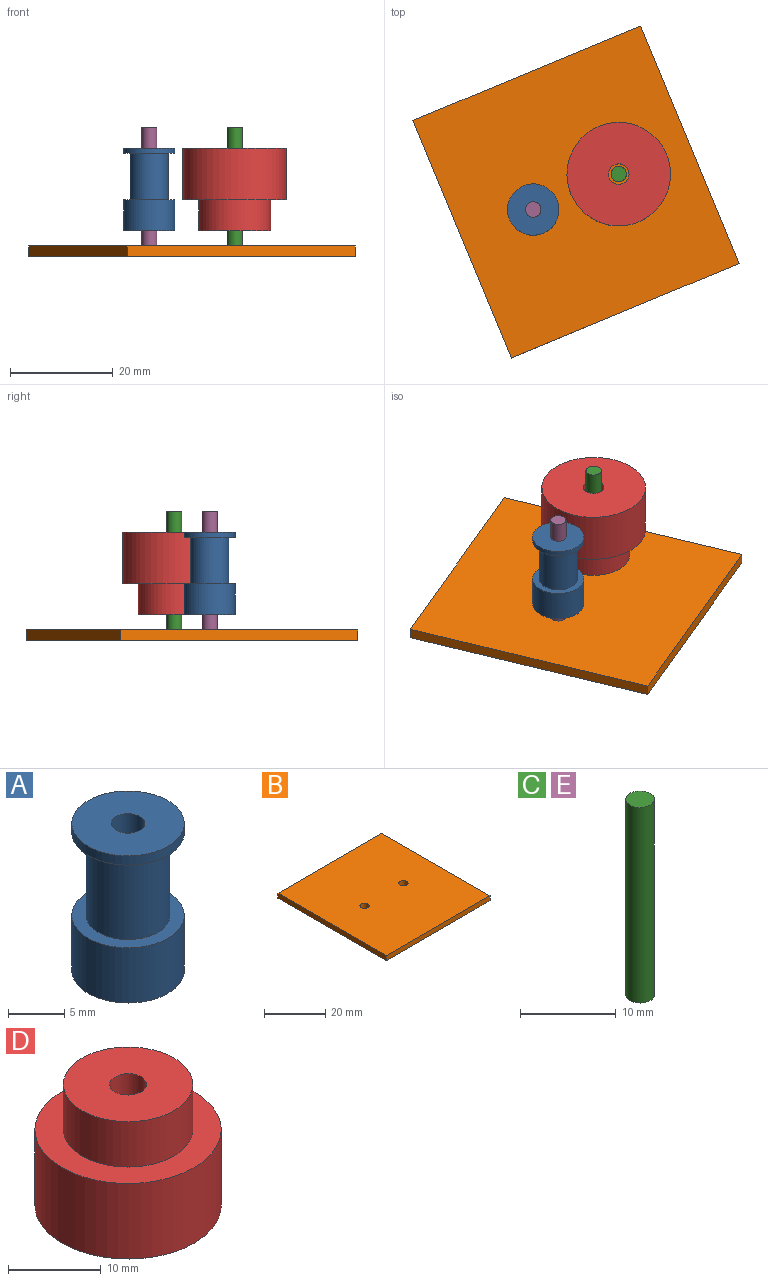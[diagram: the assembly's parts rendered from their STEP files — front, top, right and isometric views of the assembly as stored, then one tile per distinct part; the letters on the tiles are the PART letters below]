
ASSEMBLY  parts=5 mates=4
PART A: 8 faces, bbox 10x10x16 mm
  f0: cylinder r=3.73mm len=9mm, axis (0,0,1), area 210.6mm2, adj f3,f5
  f1: cylinder r=5mm len=10mm, axis (0,0,-1), area 188.5mm2, adj f2,f3
  f2: plane 10x10mm, normal (0,0,-1), area 71.5mm2, adj f1,f7
  f3: plane 10x10mm, normal (0,0,1), area 34.9mm2, adj f0,f1
  f4: cylinder r=5mm len=10mm, axis (0,0,1), area 31.4mm2, adj f5,f6
  f5: plane 10x10mm, normal (0,0,-1), area 34.9mm2, adj f0,f4
  f6: plane 10x10mm, normal (0,0,1), area 71.5mm2, adj f4,f7
  f7: cylinder r=1.5mm len=16mm, axis (0,0,1), area 150.8mm2, adj f2,f6
PART B: 8 faces, bbox 48x50x2 mm
  f0: plane 50x2mm, normal (-1,0,0), area 100mm2, adj f1,f5,f6,f7
  f1: plane 48x2mm, normal (0,1,0), area 96mm2, adj f0,f2,f6,f7
  f2: plane 50x2mm, normal (1,0,0), area 100mm2, adj f1,f5,f6,f7
  f3: cylinder r=1.5mm len=3mm, axis (0,0,1), area 18.8mm2, adj f6,f7
  f4: cylinder r=1.5mm len=3mm, axis (0,0,1), area 18.8mm2, adj f6,f7
  f5: plane 48x2mm, normal (0,-1,0), area 96mm2, adj f0,f2,f6,f7
  f6: plane 50x48mm, normal (0,0,-1), area 2385.9mm2, adj f0,f1,f2,f3,f4,f5
  f7: plane 50x48mm, normal (0,0,1), area 2385.9mm2, adj f0,f1,f2,f3,f4,f5
PART C: 3 faces, bbox 3x3x25 mm
  f0: cylinder r=1.5mm len=25mm, axis (0,0,-1), area 235.6mm2, adj f1,f2
  f1: plane 3x3mm, normal (0,0,1), area 7.1mm2, adj f0
  f2: plane 3x3mm, normal (0,0,-1), area 7.1mm2, adj f0
PART D: 6 faces, bbox 20.2x20.2x16 mm
  f0: cylinder r=10.08mm len=20.15mm, axis (0,0,-1), area 633mm2, adj f1,f3
  f1: plane 20.15x20.15mm, normal (0,0,-1), area 306.3mm2, adj f0,f5
  f2: cylinder r=7mm len=14mm, axis (0,0,1), area 263.9mm2, adj f3,f4
  f3: plane 20.15x20.15mm, normal (0,0,1), area 165mm2, adj f0,f2
  f4: plane 14x14mm, normal (0,0,1), area 141.4mm2, adj f2,f5
  f5: cylinder r=2mm len=16mm, axis (0,0,1), area 201.1mm2, adj f1,f4
PART E: same geometry as C
PLACE A t=(2.21,-9.82,-24.65)mm
PLACE B rot(axis=(0,0,-1),157.5deg) t=(10.53,-6.37,-29.65)mm
PLACE C t=(18.84,-2.92,-29.65)mm
PLACE D rot(axis=(0.2,-0.98,0),180deg) t=(18.84,-2.92,-8.65)mm
PLACE E rot(axis=(0,0,1),180deg) t=(2.21,-9.82,-29.65)mm
MATE revolute C.f0 <-> B.f4  axis (0,0,-1) through (18.84,-2.92,-29.65)mm
MATE fastened B.f4 <-> D.f5  axis (0,0,-1) through (18.84,-2.92,-29.65)mm
MATE revolute E.f0 <-> B.f3  axis (0,0,-1) through (2.21,-9.82,-29.65)mm
MATE fastened E.f0 <-> A.f7  axis (0,0,-1) through (2.21,-9.82,-29.65)mm
